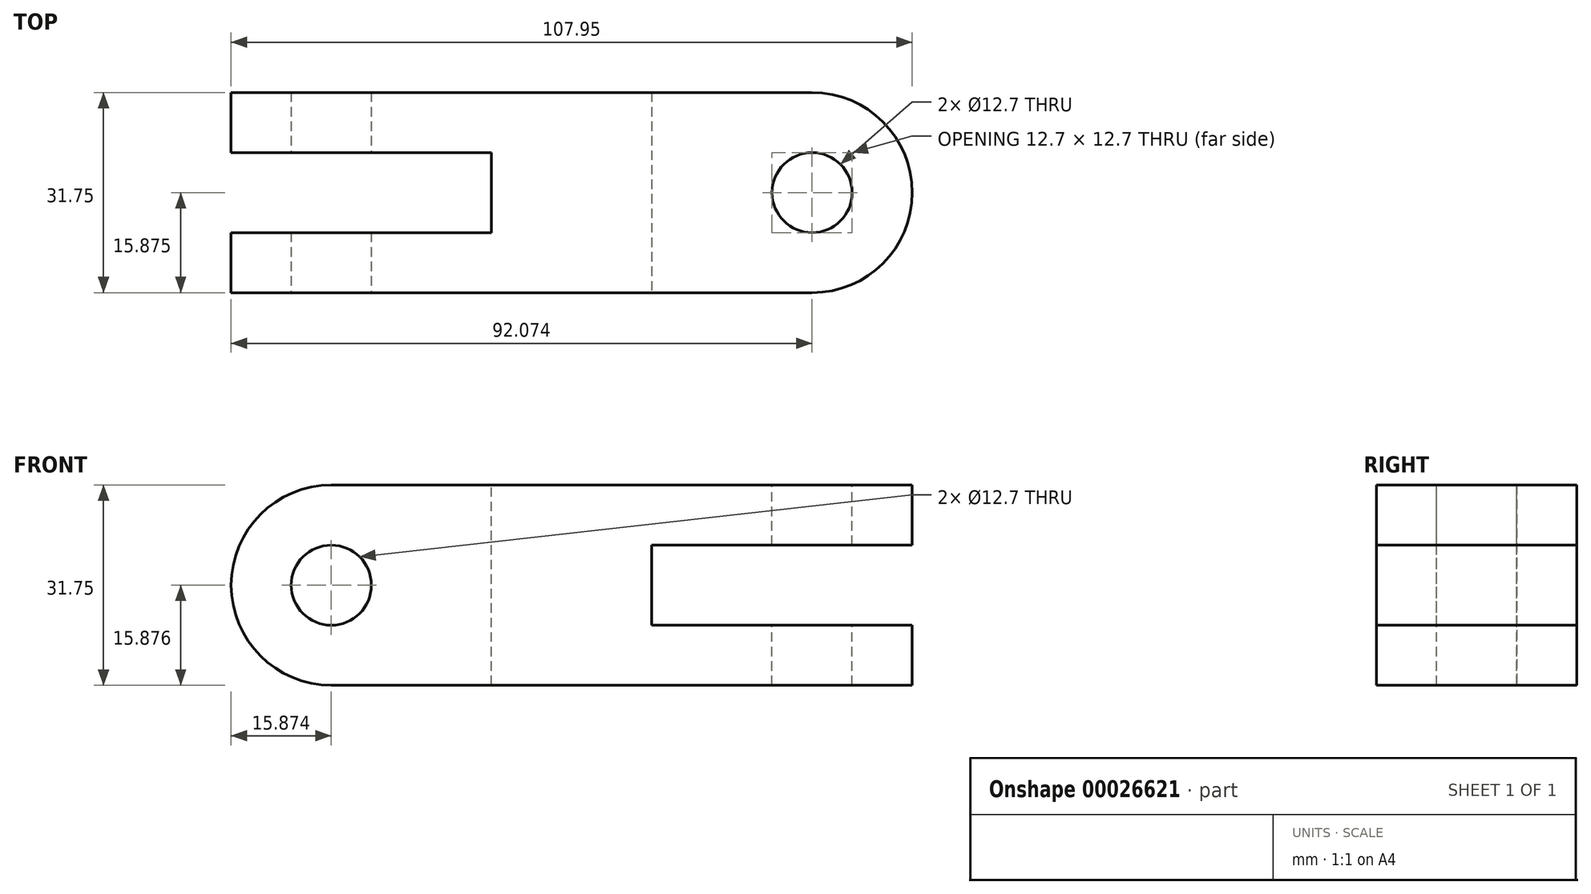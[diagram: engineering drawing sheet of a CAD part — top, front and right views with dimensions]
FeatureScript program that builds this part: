
annotation { "Feature Type Name" : "Feature", "Feature Type Description" : "" }
export const myFeature = defineFeature(function(context is Context, id is Id, definition is map)
    precondition{}
    {
        {
            var Q0;
            Q0=qCreatedBy(makeId("Front.planeOp"),FACE);
            var sketch = newSketch(context, id + "F0", { "sketchPlane" : qUnion([Q0])});
            skLineSegment(sketch, "E0", {"start": v(-39.41, 25.7) * mm, "end": v(68.54, 25.7) * mm});
            skLineSegment(sketch, "E1", {"start": v(68.54, 25.7) * mm, "end": v(68.54, -6.06) * mm});
            skLineSegment(sketch, "E2", {"start": v(68.54, -6.06) * mm, "end": v(-39.41, -6.06) * mm});
            skLineSegment(sketch, "E3", {"start": v(-39.41, -6.06) * mm, "end": v(-39.41, 25.7) * mm});
            skSolve(sketch);
        }
        {
            var Q0;
            Q0 = qSketchRegion(id + "F0", true);
            extrude(context, id + "F1", {"entities" : qUnion([Q0]), "depth" : 31.75 * mm});
        }
        {
            var Q0;
            Q0=makeQuery(id+"F1.opExtrude","CAP_FACE",FACE,{"disambiguationData":[OSD([sQuery(id+"F0.wireOp",EDGE,"E0"),sQuery(id+"F0.wireOp",EDGE,"E1"),sQuery(id+"F0.wireOp",EDGE,"E2"),sQuery(id+"F0.wireOp",EDGE,"E3")])],"isStart":false});
            var sketch = newSketch(context, id + "F2", { "sketchPlane" : qUnion([Q0])});
            skArc(sketch, "E4", {"start": v(-23.54, 25.7) * mm, "mid": v(-39.41, 9.82) * mm, "end": v(-23.54, -6.06) * mm});
            skCircle(sketch, "E5", {"center": v(-23.54, 9.82) * mm, "radius": 6.35 * mm});
            skLineSegment(sketch, "E6.0", {"start": v(27.26, 16.17) * mm, "end": v(27.26, 3.47) * mm});
            skLineSegment(sketch, "E7.0", {"start": v(68.54, 3.47) * mm, "end": v(27.26, 3.47) * mm});
            skLineSegment(sketch, "E8.trimOffspring", {"start": v(27.26, 16.17) * mm, "end": v(68.54, 16.17) * mm});
            skSolve(sketch);
        }
        {
            var Q0;
            Q0=makeQuery(id+"F2.imprint","IMPRINT",FACE,{"disambiguationData":[TD([[makeQuery(id+"F2.imprint","IMPRINT",EDGE,{"derivedFrom":sQuery(id+"F2.wireOp",EDGE,"E5")}),1.0]])]});
            var Q1;
            {var subQ1=sQuery(id+"F2.wireOp",EDGE,"E4");var subQ3=makeQuery(id+"F1.opExtrude","CAP_EDGE",EDGE,{"disambiguationData":[OSD([sQuery(id+"F0.wireOp",EDGE,"E0")])],"isStart":false});var subQ5=makeQuery(id+"F2.imprint","INTERSECT",VERTEX,{"derivedFrom":[subQ3,subQ1]});Q1=makeQuery(id+"F2.imprint","IMPRINT",FACE,{"disambiguationData":[TD([[makeQuery(id+"F2.imprint","IMPRINT",EDGE,{"disambiguationData":[TD([[subQ5,-1.0]])],"derivedFrom":subQ1}),-1.0]])]});}
            var Q2;
            {var subQ1=sQuery(id+"F2.wireOp",EDGE,"E4");var subQ3=makeQuery(id+"F1.opExtrude","CAP_EDGE",EDGE,{"disambiguationData":[OSD([sQuery(id+"F0.wireOp",EDGE,"E2")])],"isStart":false});var subQ5=makeQuery(id+"F2.imprint","INTERSECT",VERTEX,{"derivedFrom":[subQ3,subQ1]});Q2=makeQuery(id+"F2.imprint","IMPRINT",FACE,{"disambiguationData":[TD([[makeQuery(id+"F2.imprint","IMPRINT",EDGE,{"disambiguationData":[TD([[subQ5,1.0]])],"derivedFrom":subQ1}),-1.0]])]});}
            var Q3;
            Q3=makeQuery(id+"F2.imprint","IMPRINT",FACE,{"disambiguationData":[TD([[makeQuery(id+"F2.imprint","IMPRINT",EDGE,{"derivedFrom":sQuery(id+"F2.wireOp",EDGE,"E6.0")}),1.0]])]});
            extrude(context, id + "F3", {"entities" : qUnion([Q0, Q1, Q2, Q3]), "operationType" : NewBodyOperationType.REMOVE, "endBound" : BoundingType.THROUGH_ALL, "oppositeDirection" : true, "depth" : 25.4 * mm});
        }
        {
            var Q0;
            Q0=makeQuery(id+"F1.opExtrude","SWEPT_FACE",FACE,{"disambiguationData":[OSD([sQuery(id+"F0.wireOp",EDGE,"E0")])]});
            var sketch = newSketch(context, id + "F4", { "sketchPlane" : qUnion([Q0])});
            skArc(sketch, "E9", {"start": v(52.66, -31.75) * mm, "mid": v(68.54, -15.88) * mm, "end": v(52.66, 0) * mm});
            skCircle(sketch, "E10", {"center": v(52.66, -15.88) * mm, "radius": 6.35 * mm});
            skLineSegment(sketch, "E11.0", {"start": v(1.86, -9.53) * mm, "end": v(1.86, -22.22) * mm});
            skLineSegment(sketch, "E12.0", {"start": v(-23.54, -9.53) * mm, "end": v(1.86, -9.53) * mm});
            skLineSegment(sketch, "E13.0", {"start": v(-23.54, -22.23) * mm, "end": v(1.86, -22.23) * mm});
            skSolve(sketch);
        }
        {
            var Q0;
            Q0 = qSketchRegion(id + "F4", true);
            var Q1;
            Q1=makeQuery(id+"F4.imprint","IMPRINT",FACE,{"disambiguationData":[TD([[makeQuery(id+"F4.imprint","IMPRINT",EDGE,{"derivedFrom":sQuery(id+"F4.wireOp",EDGE,"E11.0")}),-1.0]])]});
            var Q2;
            {var subQ0=sQuery(id+"F0.wireOp",EDGE,"E0");var subQ1=makeQuery(id+"F1.opExtrude","CAP_EDGE",EDGE,{"disambiguationData":[OSD([subQ0])],"isStart":true});var subQ2=sQuery(id+"F4.wireOp",EDGE,"E9");var subQ3=makeQuery(id+"F4.imprint","INTERSECT",VERTEX,{"derivedFrom":[subQ1,subQ2]});Q2=makeQuery(id+"F4.imprint","IMPRINT",FACE,{"disambiguationData":[TD([[makeQuery(id+"F4.imprint","IMPRINT",EDGE,{"disambiguationData":[TD([[subQ3,1.0]])],"derivedFrom":subQ2}),-1.0]])]});}
            var Q3;
            {var subQ0=sQuery(id+"F0.wireOp",EDGE,"E0");var subQ1=makeQuery(id+"F1.opExtrude","CAP_EDGE",EDGE,{"disambiguationData":[OSD([subQ0])],"isStart":false});var subQ2=sQuery(id+"F4.wireOp",EDGE,"E9");var subQ3=makeQuery(id+"F4.imprint","INTERSECT",VERTEX,{"derivedFrom":[subQ1,subQ2]});Q3=makeQuery(id+"F4.imprint","IMPRINT",FACE,{"disambiguationData":[TD([[makeQuery(id+"F4.imprint","IMPRINT",EDGE,{"disambiguationData":[TD([[subQ3,-1.0]])],"derivedFrom":subQ2}),-1.0]])]});}
            extrude(context, id + "F5", {"entities" : qUnion([Q0, Q1, Q2, Q3]), "operationType" : NewBodyOperationType.REMOVE, "endBound" : BoundingType.THROUGH_ALL, "oppositeDirection" : true, "depth" : 25.4 * mm});
        }
        {
            var Q0;
            Q0=makeQuery(id+"F1.opExtrude","SWEPT_FACE",FACE,{"disambiguationData":[OSD([sQuery(id+"F0.wireOp",EDGE,"E0")])]});
            var sketch = newSketch(context, id + "F6", { "sketchPlane" : qUnion([Q0])});
            skLineSegment(sketch, "E14", {"start": v(-23.54, -9.53) * mm, "end": v(-46.3, -9.53) * mm});
            skLineSegment(sketch, "E15", {"start": v(-23.54, -22.22) * mm, "end": v(-45.85, -22.22) * mm});
            skLineSegment(sketch, "E16", {"start": v(-45.85, -22.22) * mm, "end": v(-46.3, -9.53) * mm});
            skSolve(sketch);
        }
        {
            var Q0;
            Q0 = qSketchRegion(id + "F6", true);
            var Q1;
            Q1=makeQuery(id+"F6.imprint","IMPRINT",FACE,{"disambiguationData":[TD([[makeQuery(id+"F6.imprint","IMPRINT",EDGE,{"derivedFrom":sQuery(id+"F6.wireOp",EDGE,"E14")}),1.0]])]});
            extrude(context, id + "F7", {"entities" : qUnion([Q0, Q1]), "operationType" : NewBodyOperationType.REMOVE, "endBound" : BoundingType.THROUGH_ALL, "oppositeDirection" : true, "depth" : 25.4 * mm});
        }
    });
